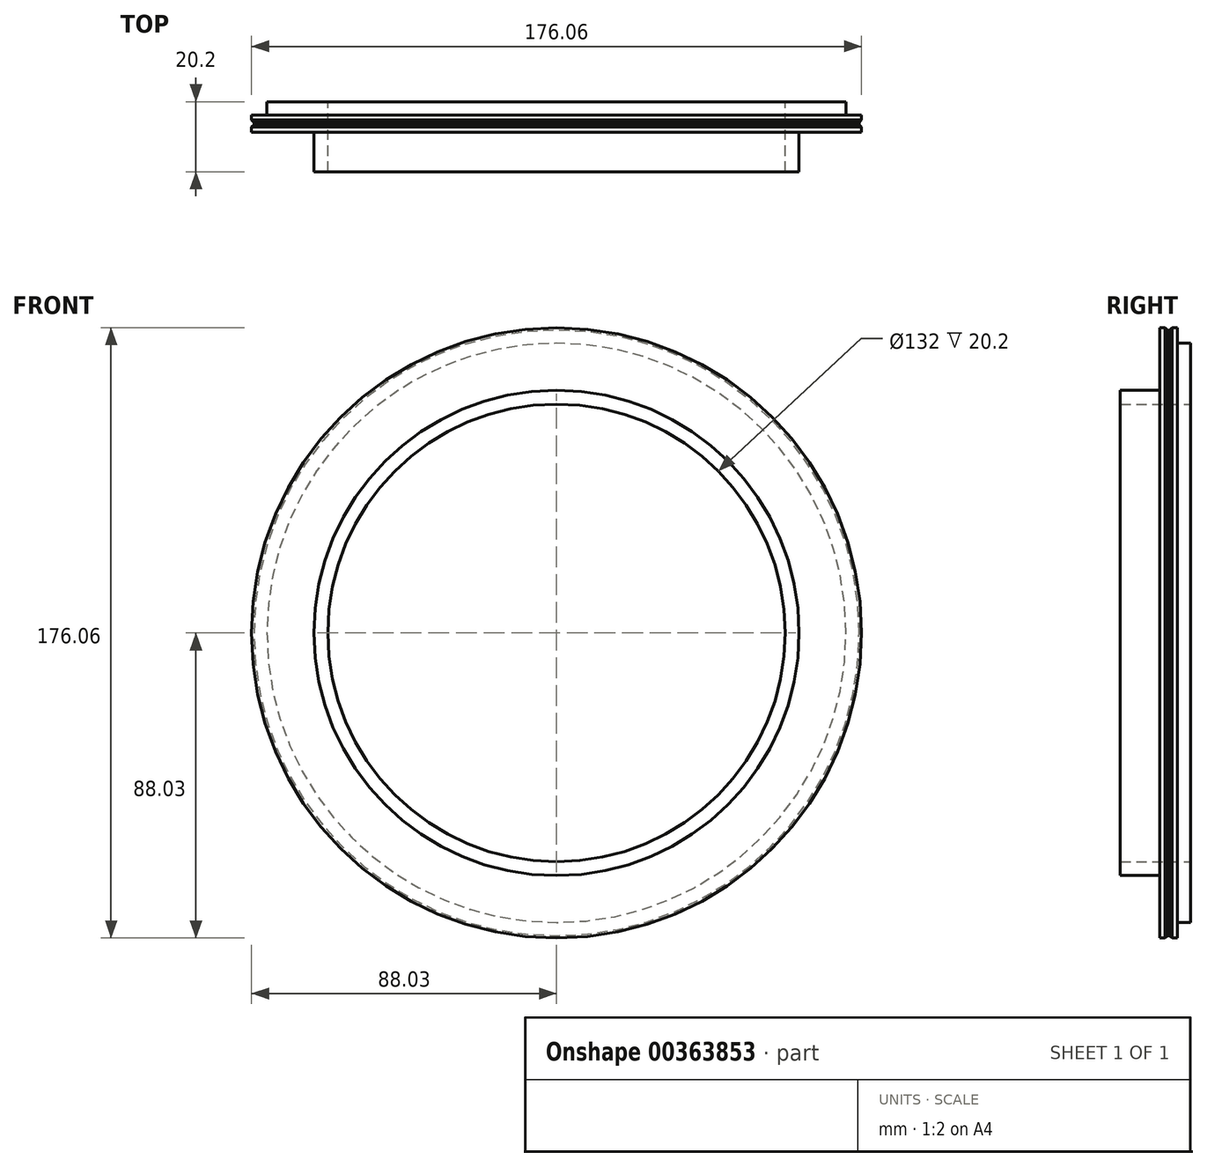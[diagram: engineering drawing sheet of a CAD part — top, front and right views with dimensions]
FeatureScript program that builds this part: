
annotation { "Feature Type Name" : "Feature", "Feature Type Description" : "" }
export const myFeature = defineFeature(function(context is Context, id is Id, definition is map)
    precondition{}
    {
        {
            var Q0;
            Q0=qCreatedBy(makeId("Right.planeOp"),FACE);
            var sketch = newSketch(context, id + "F0", { "sketchPlane" : qUnion([Q0])});
            skLineSegment(sketch, "E0", {"start": v(75.14, 0) * mm, "end": v(-75.14, 0) * mm, "construction": true});
            skLineSegment(sketch, "E1", {"start": v(75.14, 0) * mm, "end": v(75.14, 75.83) * mm});
            skLineSegment(sketch, "E2", {"start": v(4.1, 70) * mm, "end": v(15.5, 70) * mm});
            skLineSegment(sketch, "E3", {"start": v(15.5, 70) * mm, "end": v(15.5, 88.03) * mm});
            skLineSegment(sketch, "E4", {"start": v(15.5, 88.03) * mm, "end": v(17, 88.03) * mm});
            skLineSegment(sketch, "E5", {"start": v(17, 88.03) * mm, "end": v(17.7, 87.33) * mm});
            skLineSegment(sketch, "E6", {"start": v(19, 88.03) * mm, "end": v(20.5, 88.03) * mm});
            skLineSegment(sketch, "E7", {"start": v(4.1, 66) * mm, "end": v(4.1, 70) * mm});
            skLineSegment(sketch, "E8", {"start": v(19, 88.03) * mm, "end": v(18.3, 87.33) * mm});
            skLineSegment(sketch, "E9", {"start": v(18.3, 87.33) * mm, "end": v(17.7, 87.33) * mm});
            skLineSegment(sketch, "E10", {"start": v(4.1, 66) * mm, "end": v(24.3, 66) * mm});
            skLineSegment(sketch, "E11", {"start": v(24.3, 66) * mm, "end": v(24.3, 83.54) * mm});
            skLineSegment(sketch, "E12", {"start": v(24.3, 83.54) * mm, "end": v(20.5, 83.54) * mm});
            skLineSegment(sketch, "E13", {"start": v(20.5, 83.54) * mm, "end": v(20.5, 88.03) * mm});
            skSolve(sketch);
        }
        {
            var Q0;
            Q0 = qSketchRegion(id + "F0", true);
            var Q1;
            Q1=sQuery(id+"F0.wireOp",EDGE,"E0");
            revolve(context, id + "F1", {"entities" : qUnion([Q0]), "axis" : qUnion([Q1]), "revolveType" : RevolveType.FULL});
        }
    });
